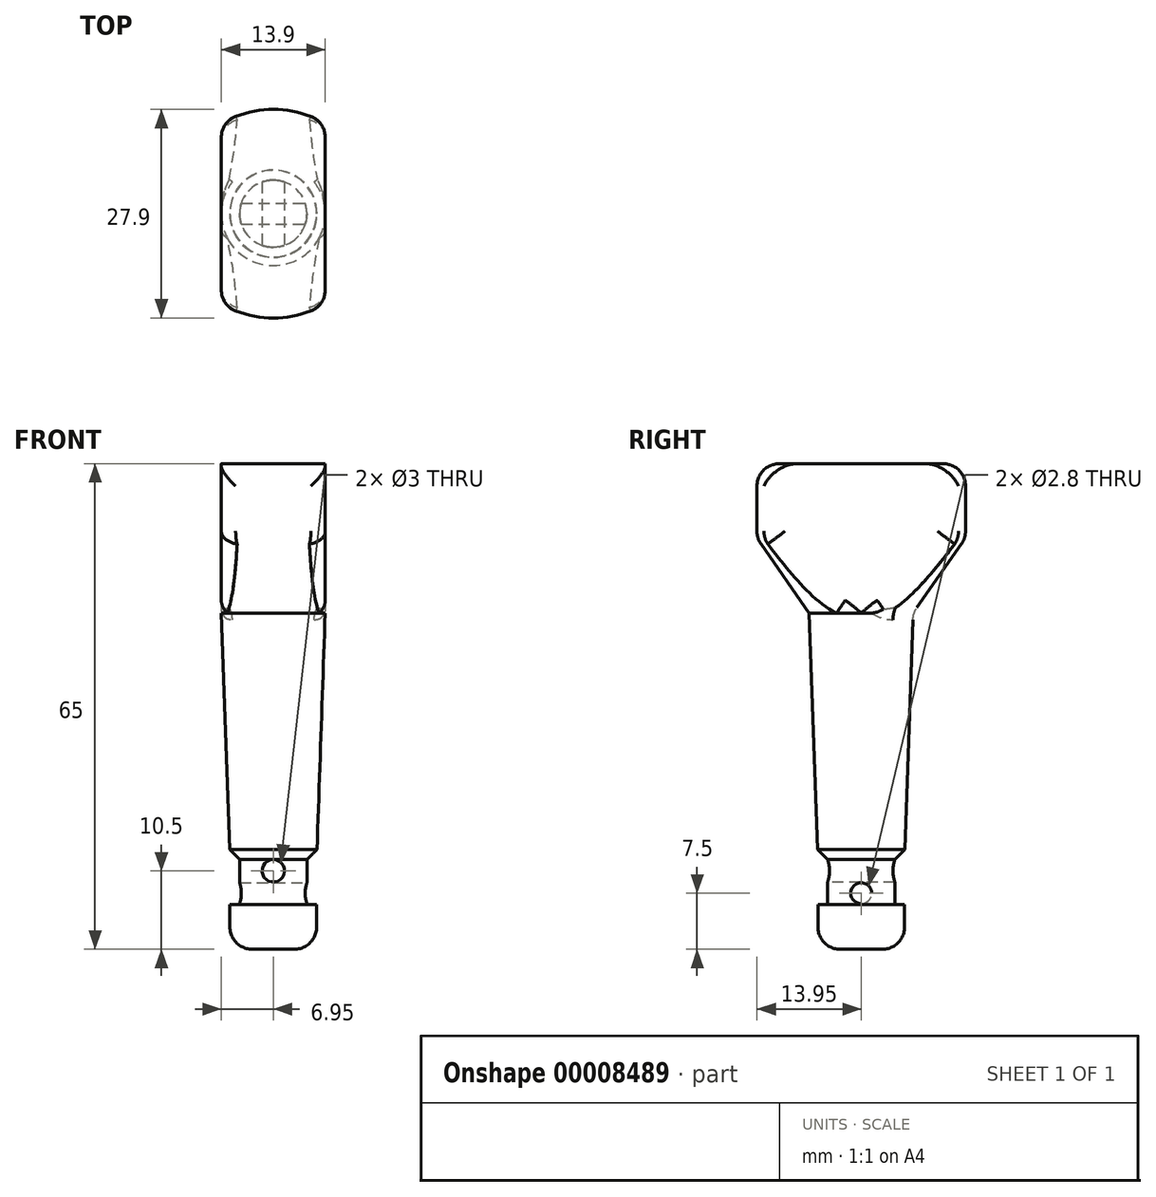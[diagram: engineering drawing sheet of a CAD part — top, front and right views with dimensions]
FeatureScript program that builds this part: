
annotation { "Feature Type Name" : "Feature", "Feature Type Description" : "" }
export const myFeature = defineFeature(function(context is Context, id is Id, definition is map)
    precondition{}
    {
        {
            var Q0;
            Q0=qCreatedBy(makeId("Front.planeOp"),FACE);
            var sketch = newSketch(context, id + "F0", { "sketchPlane" : qUnion([Q0])});
            skLineSegment(sketch, "E0.rect.bottom", {"start": v(-6.95, 45) * mm, "end": v(0, 45) * mm});
            skLineSegment(sketch, "E0.rect.top", {"start": v(-5.8, 0) * mm, "end": v(0, 0) * mm});
            skLineSegment(sketch, "E0.rect.left", {"start": v(-6.95, 45) * mm, "end": v(-5.85, 13.35) * mm});
            skPoint(sketch, "E0.rect.middle", {"position": v(0, 0) * mm});
            skLineSegment(sketch, "E1", {"start": v(0, 45) * mm, "end": v(0, 12) * mm});
            skLineSegment(sketch, "E2", {"start": v(-5.8, 6) * mm, "end": v(0, 6) * mm});
            skLineSegment(sketch, "E3", {"start": v(-4.5, 12) * mm, "end": v(0, 12) * mm});
            skLineSegment(sketch, "E4", {"start": v(-4.5, 12) * mm, "end": v(-4.5, 6) * mm});
            skLineSegment(sketch, "E5.trimOffspring", {"start": v(-5.8, 6) * mm, "end": v(-5.8, 0) * mm});
            skLineSegment(sketch, "E6", {"start": v(0, 12) * mm, "end": v(0, 6) * mm});
            skLineSegment(sketch, "E7", {"start": v(0, 6) * mm, "end": v(0, 0) * mm});
            skCircle(sketch, "E8", {"center": v(0, 10.5) * mm, "radius": 1.5 * mm});
            skLineSegment(sketch, "E9", {"start": v(-6.95, 45) * mm, "end": v(-13.95, 55) * mm});
            skLineSegment(sketch, "E10", {"start": v(-13.95, 55) * mm, "end": v(-13.95, 65) * mm});
            skLineSegment(sketch, "E11", {"start": v(-13.95, 65) * mm, "end": v(0, 65) * mm});
            skLineSegment(sketch, "E12", {"start": v(0, 65) * mm, "end": v(0, 45) * mm});
            skLineSegment(sketch, "E13", {"start": v(-6.95, 65) * mm, "end": v(-6.95, 45) * mm});
            skLineSegment(sketch, "E14.0.MirrorCS", {"start": v(6.95, 65) * mm, "end": v(6.95, 45) * mm});
            skLineSegment(sketch, "E15.0.MirrorCS", {"start": v(13.95, 65) * mm, "end": v(0, 65) * mm});
            skLineSegment(sketch, "E16.0.MirrorCS", {"start": v(13.95, 55) * mm, "end": v(13.95, 65) * mm});
            skLineSegment(sketch, "E17.0.MirrorCS", {"start": v(6.95, 45) * mm, "end": v(13.95, 55) * mm});
            skLineSegment(sketch, "E18.0.MirrorCS", {"start": v(6.95, 45) * mm, "end": v(0, 45) * mm});
            skLineSegment(sketch, "E19", {"start": v(-4.5, 12) * mm, "end": v(-5.85, 13.35) * mm});
            skPoint(sketch, "E20.orphan", {"position": v(-5.8, 12) * mm});
            skSolve(sketch);
        }
        {
            var Q0;
            Q0=makeQuery(id+"F0.imprint","IMPRINT",FACE,{"disambiguationData":[TD([[makeQuery(id+"F0.imprint","IMPRINT",EDGE,{"derivedFrom":sQuery(id+"F0.wireOp",EDGE,"E0.rect.top")}),1.0]])]});
            var Q1;
            {var subQ8=sQuery(id+"F0.wireOp",EDGE,"E4");Q1=makeQuery(id+"F0.imprint","IMPRINT",FACE,{"disambiguationData":[TD([[makeQuery(id+"F0.imprint","IMPRINT",EDGE,{"derivedFrom":subQ8}),1.0]])]});}
            var Q2;
            Q2=makeQuery(id+"F0.imprint","IMPRINT",FACE,{"disambiguationData":[TD([[makeQuery(id+"F0.imprint","IMPRINT",EDGE,{"derivedFrom":sQuery(id+"F0.wireOp",EDGE,"E0.rect.bottom")}),-1.0]])]});
            var Q3;
            Q3=makeQuery(id+"F0.imprint","IMPRINT",FACE,{"disambiguationData":[TD([[makeQuery(id+"F0.imprint","IMPRINT",EDGE,{"derivedFrom":sQuery(id+"F0.wireOp",EDGE,"E0.rect.bottom")}),1.0]])]});
            var Q4;
            {var subQ0=sQuery(id+"F0.wireOp",EDGE,"E8");var subQ1=sQuery(id+"F0.wireOp",EDGE,"E6");var subQ3=makeQuery(id+"F0.imprint","INTERSECT",VERTEX,{"disambiguationData":[OD(0.0)],"derivedFrom":[subQ1,subQ0]});Q4=makeQuery(id+"F0.imprint","IMPRINT",FACE,{"disambiguationData":[TD([[makeQuery(id+"F0.imprint","IMPRINT",EDGE,{"disambiguationData":[TD([[subQ3,-1.0]])],"derivedFrom":subQ1}),-1.0]])]});}
            var Q5;
            {var subQ3=sQuery(id+"F0.wireOp",EDGE,"E9");Q5=makeQuery(id+"F0.imprint","IMPRINT",FACE,{"disambiguationData":[TD([[makeQuery(id+"F0.imprint","IMPRINT",EDGE,{"derivedFrom":subQ3}),-1.0]])]});}
            var Q6;
            Q6=sQuery(id+"F0.wireOp",EDGE,"E1");
            revolve(context, id + "F1", {"entities" : qUnion([Q0, Q1, Q2, Q3, Q4, Q5]), "axis" : qUnion([Q6]), "revolveType" : RevolveType.FULL});
        }
        {
            var Q0;
            {var subQ0=sQuery(id+"F0.wireOp",EDGE,"E8");var subQ1=sQuery(id+"F0.wireOp",EDGE,"E6");var subQ2=makeQuery(id+"F0.imprint","INTERSECT",VERTEX,{"derivedFrom":[subQ1,subQ0]});Q0=makeQuery(id+"F0.imprint","IMPRINT",FACE,{"disambiguationData":[TD([[makeQuery(id+"F0.imprint","IMPRINT",EDGE,{"disambiguationData":[TD([[subQ2,1.0]])],"derivedFrom":subQ1}),-1.0]])]});}
            var Q1;
            {var subQ0=sQuery(id+"F0.wireOp",EDGE,"E8");var subQ1=sQuery(id+"F0.wireOp",EDGE,"E6");var subQ2=makeQuery(id+"F0.imprint","INTERSECT",VERTEX,{"derivedFrom":[subQ1,subQ0]});Q1=makeQuery(id+"F0.imprint","IMPRINT",FACE,{"disambiguationData":[TD([[makeQuery(id+"F0.imprint","IMPRINT",EDGE,{"disambiguationData":[TD([[subQ2,1.0]])],"derivedFrom":subQ1}),1.0]])]});}
            extrude(context, id + "F2", {"entities" : qUnion([Q0, Q1]), "operationType" : NewBodyOperationType.REMOVE, "endBound" : BoundingType.SYMMETRIC, "oppositeDirection" : true, "depth" : 25 * mm});
        }
        {
            var Q0;
            Q0=makeQuery(id+"F1.opRevolve","SWEPT_EDGE",EDGE,{"disambiguationData":[OSD([sQuery(id+"F0.wireOp",EDGE,"E0.rect.top"),sQuery(id+"F0.wireOp",EDGE,"E5.trimOffspring")])]});
            fillet(context, id + "F3", {"entities" : qUnion([Q0]), "radius" : 3 * mm, "tangentPropagation" : true, "allowEdgeOverflow" : false});
        }
        {
            var Q0;
            {var subQ3=sQuery(id+"F0.wireOp",EDGE,"E9");Q0=makeQuery(id+"F0.imprint","IMPRINT",FACE,{"disambiguationData":[TD([[makeQuery(id+"F0.imprint","IMPRINT",EDGE,{"derivedFrom":subQ3}),-1.0]])]});}
            var Q1;
            {var subQ2=sQuery(id+"F0.wireOp",EDGE,"E14.0.MirrorCS");Q1=makeQuery(id+"F0.imprint","IMPRINT",FACE,{"disambiguationData":[TD([[makeQuery(id+"F0.imprint","IMPRINT",EDGE,{"derivedFrom":subQ2}),1.0]])]});}
            extrude(context, id + "F4", {"entities" : qUnion([Q0, Q1]), "operationType" : NewBodyOperationType.REMOVE, "endBound" : BoundingType.SYMMETRIC, "oppositeDirection" : true, "depth" : 25 * mm});
        }
        {
            var Q0;
            Q0=makeQuery(id+"F4.boolean.opBoolean","SPLIT",EDGE,{"disambiguationData":[OD(0.0)],"derivedFrom":makeQuery(id+"F1.opRevolve","SWEPT_EDGE",EDGE,{"disambiguationData":[OSD([sQuery(id+"F0.wireOp",EDGE,"E10"),sQuery(id+"F0.wireOp",EDGE,"E11")])]})});
            var Q1;
            Q1=makeQuery(id+"F4.boolean.opBoolean","COPY",EDGE,{"derivedFrom":makeQuery(id+"F4.opExtrude","SWEPT_EDGE",EDGE,{"disambiguationData":[OSD([sQuery(id+"F0.wireOp",EDGE,"E14.0.MirrorCS"),sQuery(id+"F0.wireOp",EDGE,"E15.0.MirrorCS")])]})});
            var Q2;
            Q2=makeQuery(id+"F4.boolean.opBoolean","SPLIT",EDGE,{"disambiguationData":[OD(1.0)],"derivedFrom":makeQuery(id+"F1.opRevolve","SWEPT_EDGE",EDGE,{"disambiguationData":[OSD([sQuery(id+"F0.wireOp",EDGE,"E10"),sQuery(id+"F0.wireOp",EDGE,"E11")])]})});
            var Q3;
            Q3=makeQuery(id+"F4.boolean.opBoolean","COPY",EDGE,{"derivedFrom":makeQuery(id+"F4.opExtrude","SWEPT_EDGE",EDGE,{"disambiguationData":[OSD([sQuery(id+"F0.wireOp",EDGE,"E11"),sQuery(id+"F0.wireOp",EDGE,"E13")])]})});
            var Q4;
            Q4=makeQuery(id+"F4.boolean.opBoolean","INTERSECT",EDGE,{"disambiguationData":[OD(0.0)],"derivedFrom":[makeQuery(id+"F1.opRevolve","SWEPT_FACE",FACE,{"disambiguationData":[OSD([sQuery(id+"F0.wireOp",EDGE,"E10")])]}),makeQuery(id+"F4.opExtrude","SWEPT_FACE",FACE,{"disambiguationData":[OSD([sQuery(id+"F0.wireOp",EDGE,"E14.0.MirrorCS")])]})]});
            var Q5;
            Q5=makeQuery(id+"F4.boolean.opBoolean","INTERSECT",EDGE,{"disambiguationData":[OD(1.0)],"derivedFrom":[makeQuery(id+"F1.opRevolve","SWEPT_FACE",FACE,{"disambiguationData":[OSD([sQuery(id+"F0.wireOp",EDGE,"E10")])]}),makeQuery(id+"F4.opExtrude","SWEPT_FACE",FACE,{"disambiguationData":[OSD([sQuery(id+"F0.wireOp",EDGE,"E14.0.MirrorCS")])]})]});
            var Q6;
            Q6=makeQuery(id+"F4.boolean.opBoolean","INTERSECT",EDGE,{"disambiguationData":[OD(1.0)],"derivedFrom":[makeQuery(id+"F1.opRevolve","SWEPT_FACE",FACE,{"disambiguationData":[OSD([sQuery(id+"F0.wireOp",EDGE,"E10")])]}),makeQuery(id+"F4.opExtrude","SWEPT_FACE",FACE,{"disambiguationData":[OSD([sQuery(id+"F0.wireOp",EDGE,"E13")])]})]});
            var Q7;
            Q7=makeQuery(id+"F4.boolean.opBoolean","INTERSECT",EDGE,{"disambiguationData":[OD(0.0)],"derivedFrom":[makeQuery(id+"F1.opRevolve","SWEPT_FACE",FACE,{"disambiguationData":[OSD([sQuery(id+"F0.wireOp",EDGE,"E10")])]}),makeQuery(id+"F4.opExtrude","SWEPT_FACE",FACE,{"disambiguationData":[OSD([sQuery(id+"F0.wireOp",EDGE,"E13")])]})]});
            var Q8;
            Q8=makeQuery(id+"F4.boolean.opBoolean","SPLIT",EDGE,{"disambiguationData":[OD(0.0)],"derivedFrom":makeQuery(id+"F1.opRevolve","SWEPT_EDGE",EDGE,{"disambiguationData":[OSD([sQuery(id+"F0.wireOp",EDGE,"E9"),sQuery(id+"F0.wireOp",EDGE,"E10")])]})});
            var Q9;
            Q9=makeQuery(id+"F4.boolean.opBoolean","SPLIT",EDGE,{"disambiguationData":[OD(1.0)],"derivedFrom":makeQuery(id+"F1.opRevolve","SWEPT_EDGE",EDGE,{"disambiguationData":[OSD([sQuery(id+"F0.wireOp",EDGE,"E9"),sQuery(id+"F0.wireOp",EDGE,"E10")])]})});
            var Q10;
            Q10=makeQuery(id+"F4.boolean.opBoolean","INTERSECT",EDGE,{"disambiguationData":[OD(1.0)],"derivedFrom":[makeQuery(id+"F1.opRevolve","SWEPT_FACE",FACE,{"disambiguationData":[OSD([sQuery(id+"F0.wireOp",EDGE,"E9")])]}),makeQuery(id+"F4.opExtrude","SWEPT_FACE",FACE,{"disambiguationData":[OSD([sQuery(id+"F0.wireOp",EDGE,"E13")])]})]});
            var Q11;
            Q11=makeQuery(id+"F4.boolean.opBoolean","INTERSECT",EDGE,{"disambiguationData":[OD(0.0)],"derivedFrom":[makeQuery(id+"F1.opRevolve","SWEPT_FACE",FACE,{"disambiguationData":[OSD([sQuery(id+"F0.wireOp",EDGE,"E9")])]}),makeQuery(id+"F4.opExtrude","SWEPT_FACE",FACE,{"disambiguationData":[OSD([sQuery(id+"F0.wireOp",EDGE,"E14.0.MirrorCS")])]})]});
            fillet(context, id + "F5", {"entities" : qUnion([Q0, Q1, Q2, Q3, Q4, Q5, Q6, Q7, Q8, Q9, Q10, Q11]), "radius" : 3 * mm, "tangentPropagation" : true, "allowEdgeOverflow" : false});
        }
        {
            var Q0;
            Q0=makeQuery(id+"F4.boolean.opBoolean","SPLIT",EDGE,{"disambiguationData":[OD(1.0)],"derivedFrom":makeQuery(id+"F1.opRevolve","SWEPT_EDGE",EDGE,{"disambiguationData":[OSD([sQuery(id+"F0.wireOp",EDGE,"E0.rect.bottom"),sQuery(id+"F0.wireOp",EDGE,"E0.rect.left"),sQuery(id+"F0.wireOp",EDGE,"E9"),sQuery(id+"F0.wireOp",EDGE,"E13")])]})});
            fillet(context, id + "F6", {"entities" : qUnion([Q0]), "radius" : 3 * mm, "tangentPropagation" : true, "allowEdgeOverflow" : false});
        }
        {
            var Q0;
            {var subQ0=sQuery(id+"F0.wireOp",EDGE,"E8");var subQ1=sQuery(id+"F0.wireOp",EDGE,"E6");var subQ2=makeQuery(id+"F0.imprint","INTERSECT",VERTEX,{"derivedFrom":[subQ1,subQ0]});Q0=makeQuery(id+"F0.imprint","IMPRINT",FACE,{"disambiguationData":[TD([[makeQuery(id+"F0.imprint","IMPRINT",EDGE,{"disambiguationData":[TD([[subQ2,1.0]])],"derivedFrom":subQ1}),1.0]])]});}
            var Q1;
            {var subQ0=sQuery(id+"F0.wireOp",EDGE,"E8");var subQ1=sQuery(id+"F0.wireOp",EDGE,"E6");var subQ2=makeQuery(id+"F0.imprint","INTERSECT",VERTEX,{"derivedFrom":[subQ1,subQ0]});Q1=makeQuery(id+"F0.imprint","IMPRINT",FACE,{"disambiguationData":[TD([[makeQuery(id+"F0.imprint","IMPRINT",EDGE,{"disambiguationData":[TD([[subQ2,1.0]])],"derivedFrom":subQ1}),-1.0]])]});}
            extrude(context, id + "F7", {"entities" : qUnion([Q0, Q1]), "endBound" : BoundingType.SYMMETRIC, "depth" : 25 * mm});
        }
        {
            var Q0;
            Q0=makeQuery(id+"F7.opExtrude","SWEPT_BODY",BODY,{"disambiguationData":[OSD([sQuery(id+"F0.wireOp",EDGE,"E8")])]});
            transform(context, id + "F8", {"entities" : qUnion([Q0]), "transformType" : TransformType.TRANSLATION_3D, "dx" : 0 * mm, "dy" : 0 * mm, "dz" : -3 * mm, "makeCopy" : false});
        }
        {
            var Q0;
            Q0=makeQuery(id+"F7.opExtrude","SWEPT_BODY",BODY,{"disambiguationData":[OSD([sQuery(id+"F0.wireOp",EDGE,"E8")])]});
            var Q1;
            Q1=sQuery(id+"F0.wireOp",EDGE,"E6");
            transform(context, id + "F9", {"entities" : qUnion([Q0]), "transformType" : TransformType.ROTATION, "transformAxis" : qUnion([Q1]), "angle" : 90 * degree, "makeCopy" : false});
        }
        {
            var Q0;
            Q0=makeQuery(id+"F7.opExtrude","SWEPT_BODY",BODY,{"disambiguationData":[OSD([sQuery(id+"F0.wireOp",EDGE,"E8")])]});
            var Q1;
            Q1=makeQuery(id+"F1.opRevolve","SWEPT_BODY",BODY,{"disambiguationData":[OSD([sQuery(id+"F0.wireOp",EDGE,"E0.rect.top"),sQuery(id+"F0.wireOp",EDGE,"E0.rect.left"),sQuery(id+"F0.wireOp",EDGE,"E1"),sQuery(id+"F0.wireOp",EDGE,"E2"),sQuery(id+"F0.wireOp",EDGE,"E4"),sQuery(id+"F0.wireOp",EDGE,"E5.trimOffspring"),sQuery(id+"F0.wireOp",EDGE,"E6"),sQuery(id+"F0.wireOp",EDGE,"E7"),sQuery(id+"F0.wireOp",EDGE,"E8"),sQuery(id+"F0.wireOp",EDGE,"E9"),sQuery(id+"F0.wireOp",EDGE,"E10"),sQuery(id+"F0.wireOp",EDGE,"E11"),sQuery(id+"F0.wireOp",EDGE,"E12"),sQuery(id+"F0.wireOp",EDGE,"E19")])]});
            booleanBodies(context, id + "F10", {"operationType" : BooleanOperationType.SUBTRACTION, "tools" : qUnion([Q0]), "targets" : qUnion([Q1]), "offset" : true, "offsetAll" : true, "offsetDistance" : 0.1 * mm, "oppositeDirection" : true});
        }
    });
